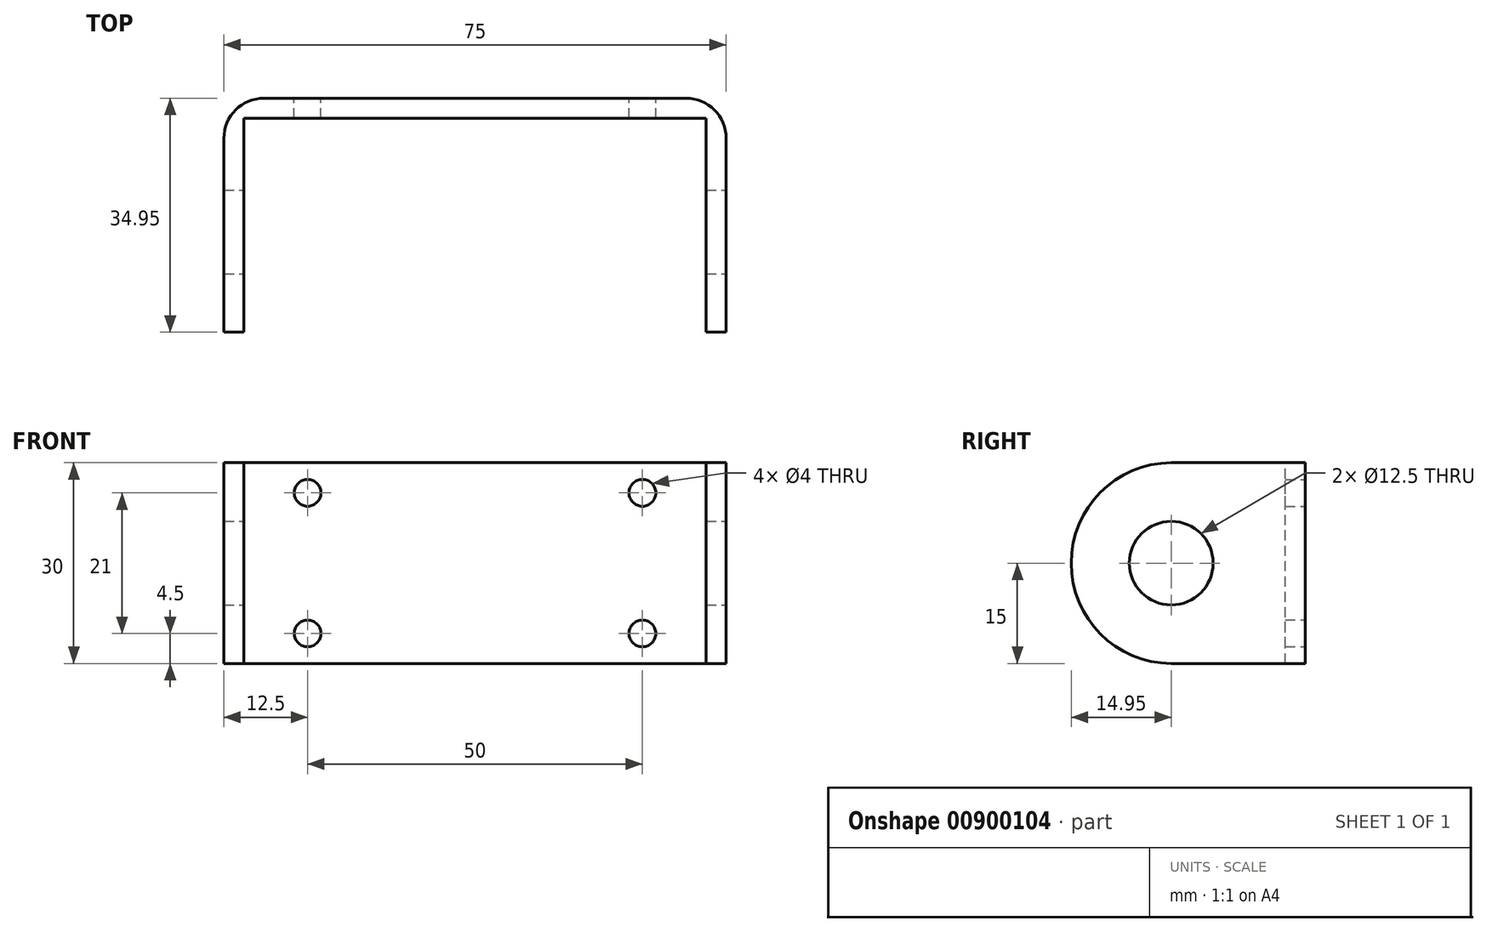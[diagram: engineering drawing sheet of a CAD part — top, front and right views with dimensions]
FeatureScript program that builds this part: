
annotation { "Feature Type Name" : "Feature", "Feature Type Description" : "" }
export const myFeature = defineFeature(function(context is Context, id is Id, definition is map)
    precondition{}
    {
        {
            var Q0;
            Q0=qCreatedBy(makeId("Front.planeOp"),FACE);
            var sketch = newSketch(context, id + "F0", { "sketchPlane" : qUnion([Q0])});
            skLineSegment(sketch, "E0.bottom", {"start": v(37.5, -15) * mm, "end": v(-37.5, -15) * mm});
            skLineSegment(sketch, "E0.top", {"start": v(37.5, 15) * mm, "end": v(-37.5, 15) * mm});
            skLineSegment(sketch, "E0.left", {"start": v(37.5, -15) * mm, "end": v(37.5, 15) * mm});
            skLineSegment(sketch, "E0.right", {"start": v(-37.5, -15) * mm, "end": v(-37.5, 15) * mm});
            skPoint(sketch, "E0.middle", {"position": v(0, 0) * mm});
            skLineSegment(sketch, "E1", {"start": v(0, 18.45) * mm, "end": v(0, 28.99) * mm, "construction": true});
            skLineSegment(sketch, "E2", {"start": v(0, 18.45) * mm, "end": v(25, 18.45) * mm, "construction": true});
            skLineSegment(sketch, "E3", {"start": v(25, 15) * mm, "end": v(25, 10.5) * mm, "construction": true});
            skCircle(sketch, "E4", {"center": v(25, 10.5) * mm, "radius": 2 * mm});
            skLineSegment(sketch, "E5", {"start": v(25, -15) * mm, "end": v(25, -10.5) * mm, "construction": true});
            skCircle(sketch, "E6", {"center": v(25, -10.5) * mm, "radius": 2 * mm});
            skLineSegment(sketch, "E7", {"start": v(25, 10.5) * mm, "end": v(25, -10.5) * mm, "construction": true});
            skLineSegment(sketch, "E8", {"start": v(0, 18.45) * mm, "end": v(-25, 18.45) * mm, "construction": true});
            skLineSegment(sketch, "E9", {"start": v(-25, 10.5) * mm, "end": v(-25, -10.5) * mm, "construction": true});
            skCircle(sketch, "E10", {"center": v(-25, 10.5) * mm, "radius": 2 * mm});
            skCircle(sketch, "E11", {"center": v(-25, -10.5) * mm, "radius": 2 * mm});
            skSolve(sketch);
        }
        {
            var Q0;
            Q0 = qSketchRegion(id + "F0", true);
            extrude(context, id + "F1", {"entities" : qUnion([Q0]), "depth" : 3 * mm, "offsetDistance" : 25 * mm});
        }
        {
            var Q0;
            Q0=makeQuery(id+"F1.opExtrude","CAP_FACE",FACE,{"disambiguationData":[OSD([sQuery(id+"F0.wireOp",EDGE,"E0.bottom"),sQuery(id+"F0.wireOp",EDGE,"E0.top"),sQuery(id+"F0.wireOp",EDGE,"E0.left"),sQuery(id+"F0.wireOp",EDGE,"E0.right"),sQuery(id+"F0.wireOp",EDGE,"E4"),sQuery(id+"F0.wireOp",EDGE,"E6"),sQuery(id+"F0.wireOp",EDGE,"E10"),sQuery(id+"F0.wireOp",EDGE,"E11")])],"isStart":false});
            var sketch = newSketch(context, id + "F2", { "sketchPlane" : qUnion([Q0])});
            skLineSegment(sketch, "E12", {"start": v(-37.5, 15.92) * mm, "end": v(-34.5, 15.92) * mm, "construction": true});
            skLineSegment(sketch, "E13", {"start": v(-34.5, -15) * mm, "end": v(-34.5, 15) * mm});
            skLineSegment(sketch, "E14", {"start": v(37.5, 16.25) * mm, "end": v(34.5, 16.25) * mm, "construction": true});
            skLineSegment(sketch, "E15", {"start": v(34.5, -15) * mm, "end": v(34.5, 15) * mm});
            skSolve(sketch);
        }
        {
            var Q0;
            {var subQ0=sQuery(id+"F2.wireOp",EDGE,"E13");Q0=makeQuery(id+"F2.imprint","IMPRINT",FACE,{"disambiguationData":[TD([[makeQuery(id+"F2.imprint","IMPRINT",EDGE,{"derivedFrom":subQ0}),1.0]])]});}
            var Q1;
            {var subQ0=sQuery(id+"F2.wireOp",EDGE,"E15");Q1=makeQuery(id+"F2.imprint","IMPRINT",FACE,{"disambiguationData":[TD([[makeQuery(id+"F2.imprint","IMPRINT",EDGE,{"derivedFrom":subQ0}),-1.0]])]});}
            extrude(context, id + "F3", {"entities" : qUnion([Q0, Q1]), "operationType" : NewBodyOperationType.ADD, "depth" : 37 * mm, "offsetDistance" : 25 * mm});
        }
        {
            var Q0;
            {var subQ0=sQuery(id+"F0.wireOp",EDGE,"E0.left");Q0=makeQuery(id+"F3.boolean.opBoolean","MERGE",FACE,{"derivedFrom":[makeQuery(id+"F1.opExtrude","SWEPT_FACE",FACE,{"disambiguationData":[OSD([subQ0])]}),makeQuery(id+"F3.opExtrude","SWEPT_FACE",FACE,{"disambiguationData":[OSD([subQ0])]})]});}
            var sketch = newSketch(context, id + "F4", { "sketchPlane" : qUnion([Q0])});
            skLineSegment(sketch, "E16", {"start": v(0, 20.01) * mm, "end": v(-20, 20.01) * mm, "construction": true});
            skLineSegment(sketch, "E17", {"start": v(-20, 15) * mm, "end": v(-20, -15) * mm, "construction": true});
            skCircle(sketch, "E18", {"center": v(-20, 0) * mm, "radius": 6.25 * mm});
            skLineSegment(sketch, "E19", {"start": v(-40, 0) * mm, "end": v(0, 0) * mm, "construction": true});
            skArc(sketch, "E20", {"start": v(-20, 15) * mm, "mid": v(-34.95, 0) * mm, "end": v(-20, -15) * mm});
            skSolve(sketch);
        }
        {
            var Q0;
            Q0 = qSketchRegion(id + "F4", true);
            var Q1;
            {var subQ0=sQuery(id+"F4.wireOp",EDGE,"E20");Q1=makeQuery(id+"F4.imprint","IMPRINT",FACE,{"disambiguationData":[TD([[makeQuery(id+"F4.imprint","IMPRINT",EDGE,{"derivedFrom":subQ0}),-1.0]])]});}
            extrude(context, id + "F5", {"entities" : qUnion([Q0, Q1]), "operationType" : NewBodyOperationType.REMOVE, "oppositeDirection" : true, "depth" : 2500 * mm, "offsetDistance" : 25 * mm});
        }
        {
            var Q0;
            Q0=makeQuery(id+"F1.opExtrude","CAP_EDGE",EDGE,{"disambiguationData":[OSD([sQuery(id+"F0.wireOp",EDGE,"E0.left")])],"isStart":true});
            var Q1;
            Q1=makeQuery(id+"F1.opExtrude","CAP_EDGE",EDGE,{"disambiguationData":[OSD([sQuery(id+"F0.wireOp",EDGE,"E0.right")])],"isStart":true});
            var Q2;
            Q2=makeQuery(id+"F3.opExtrude","CAP_EDGE",EDGE,{"disambiguationData":[OSD([sQuery(id+"F2.wireOp",EDGE,"E13")])],"isStart":true});
            var Q3;
            Q3=makeQuery(id+"F3.opExtrude","CAP_EDGE",EDGE,{"disambiguationData":[OSD([sQuery(id+"F2.wireOp",EDGE,"E15")])],"isStart":true});
            fillet(context, id + "F6", {"entities" : qUnion([Q0, Q1, Q2, Q3]), "radius" : 6 * mm, "tangentPropagation" : true, "allowEdgeOverflow" : false});
        }
    });
